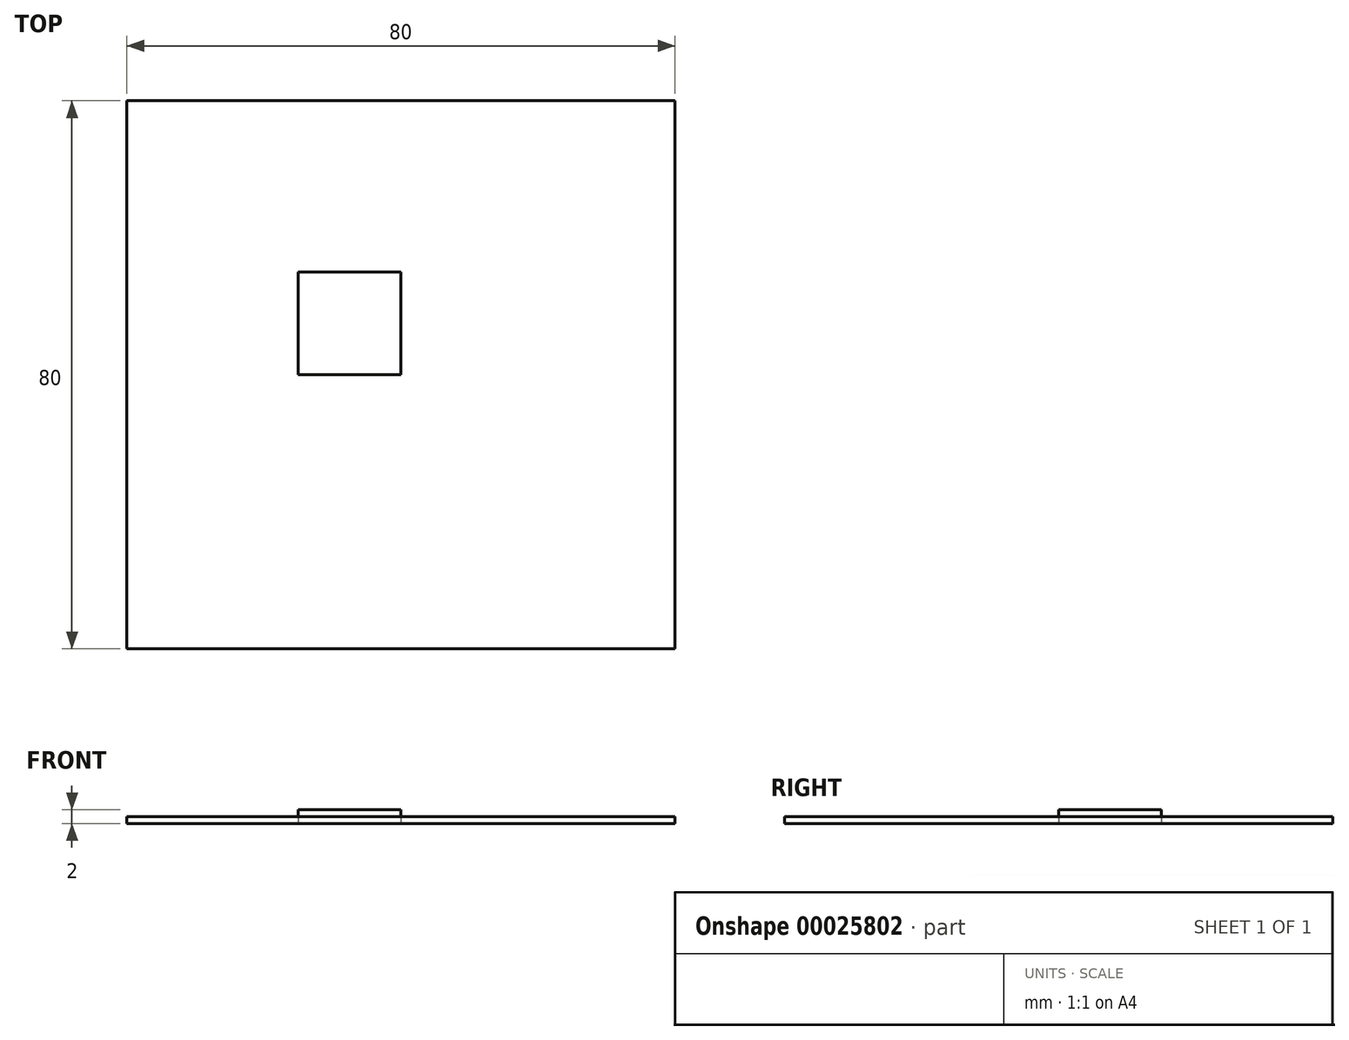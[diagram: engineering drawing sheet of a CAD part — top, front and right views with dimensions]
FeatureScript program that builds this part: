
annotation { "Feature Type Name" : "Feature", "Feature Type Description" : "" }
export const myFeature = defineFeature(function(context is Context, id is Id, definition is map)
    precondition{}
    {
        {
            var Q0;
            Q0=qCreatedBy(makeId("Top.planeOp"),FACE);
            var sketch = newSketch(context, id + "F0", { "sketchPlane" : qUnion([Q0])});
            skLineSegment(sketch, "E0.rect.bottom", {"start": v(-40, 40) * mm, "end": v(40, 40) * mm});
            skLineSegment(sketch, "E0.rect.top", {"start": v(-40, -40) * mm, "end": v(40, -40) * mm});
            skLineSegment(sketch, "E0.rect.left", {"start": v(-40, 40) * mm, "end": v(-40, -40) * mm});
            skLineSegment(sketch, "E0.rect.right", {"start": v(40, 40) * mm, "end": v(40, -40) * mm});
            skPoint(sketch, "E0.rect.middle", {"position": v(0, 0) * mm});
            skLineSegment(sketch, "E1.bottom", {"start": v(0, 0) * mm, "end": v(-15, 0) * mm});
            skLineSegment(sketch, "E1.top", {"start": v(0, -15) * mm, "end": v(-15, -15) * mm});
            skLineSegment(sketch, "E1.left", {"start": v(0, 0) * mm, "end": v(0, -15) * mm});
            skLineSegment(sketch, "E1.right", {"start": v(-15, 0) * mm, "end": v(-15, -15) * mm});
            skSolve(sketch);
        }
        {
            var Q0;
            Q0=makeQuery(id+"F0.imprint","IMPRINT",FACE,{"disambiguationData":[TD([[makeQuery(id+"F0.imprint","IMPRINT",EDGE,{"derivedFrom":sQuery(id+"F0.wireOp",EDGE,"E0.rect.bottom")}),-1.0]])]});
            var Q1;
            Q1=makeQuery(id+"F0.imprint","IMPRINT",FACE,{"disambiguationData":[TD([[makeQuery(id+"F0.imprint","IMPRINT",EDGE,{"derivedFrom":sQuery(id+"F0.wireOp",EDGE,"E1.bottom")}),1.0]])]});
            extrude(context, id + "F1", {"entities" : qUnion([Q0, Q1]), "depth" : 1 * mm});
        }
        {
            var Q0;
            Q0=qCreatedBy(makeId("Top.planeOp"),FACE);
            var sketch = newSketch(context, id + "F2", { "sketchPlane" : qUnion([Q0])});
            skLineSegment(sketch, "E2.bottom", {"start": v(0, 0) * mm, "end": v(-15, 0) * mm});
            skLineSegment(sketch, "E2.top", {"start": v(0, 15) * mm, "end": v(-15, 15) * mm});
            skLineSegment(sketch, "E2.left", {"start": v(0, 0) * mm, "end": v(0, 15) * mm});
            skLineSegment(sketch, "E2.right", {"start": v(-15, 0) * mm, "end": v(-15, 15) * mm});
            skSolve(sketch);
        }
        {
            var Q0;
            Q0=makeQuery(id+"F2.imprint","IMPRINT",FACE,{"disambiguationData":[TD([[makeQuery(id+"F2.imprint","IMPRINT",EDGE,{"derivedFrom":sQuery(id+"F2.wireOp",EDGE,"E2.bottom")}),-1.0]])]});
            extrude(context, id + "F3", {"entities" : qUnion([Q0]), "depth" : 2 * mm});
        }
    });
